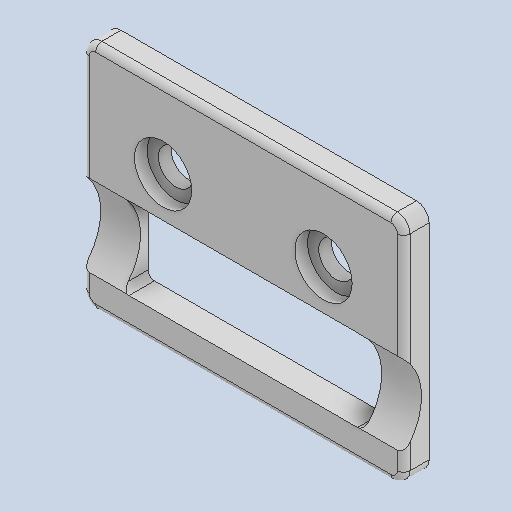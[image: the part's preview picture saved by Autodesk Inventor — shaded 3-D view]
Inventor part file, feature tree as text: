
AUTODESK INVENTOR PART (.ipt)
format: ipt  version: 2022 (Build 260153000, 153)  size: 156,672 bytes
history: native  units: in
note: dims shown in document units (in); Inventor stores cm internally (conversion verified against a paired STEP export)
features: fillet x1
ambient origin geometry x8: Origin, YZ Plane, XZ Plane, XY Plane, X Axis, Y Axis, Z Axis, Center Point
bodies: Solid1 (feature_tree)
feature tree (1):
  fillet  "Fillet2"  [1 undecoded]
note: 1 required parameter value undecoded (feature->parameter linkage not recoverable at this tier; creation-order binding heuristic only, values carry confidence <= 0.55)
